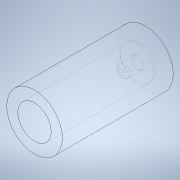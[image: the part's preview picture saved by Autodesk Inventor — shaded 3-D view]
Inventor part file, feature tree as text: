
AUTODESK INVENTOR PART (.ipt)
format: ipt  version: 2022 (Build 260153000, 153)  size: 96,768 bytes
history: native  units: mm (DEFAULTED — no unit token found)
features: sketch x2, extrude x1, revolve x1
ambient origin geometry x8: Origin, YZ Plane, XZ Plane, XY Plane, X Axis, Y Axis, Z Axis, Center Point
bodies: Solid1 (feature_tree)
feature tree (4):
  sketch  "Sketch1"  dims[d0=0.0mm d1=50.8mm d2=50.8mm d3=0.0mm]
  sketch  "Sketch2"  dims[d4=0.0mm]
  extrude  "Extrusion1"  Depth=50.8mm TaperAngle=0.0deg
  revolve  "Revolution1"  [1 undecoded]
note: 1 required parameter value undecoded (feature->parameter linkage not recoverable at this tier; creation-order binding heuristic only, values carry confidence <= 0.55)
